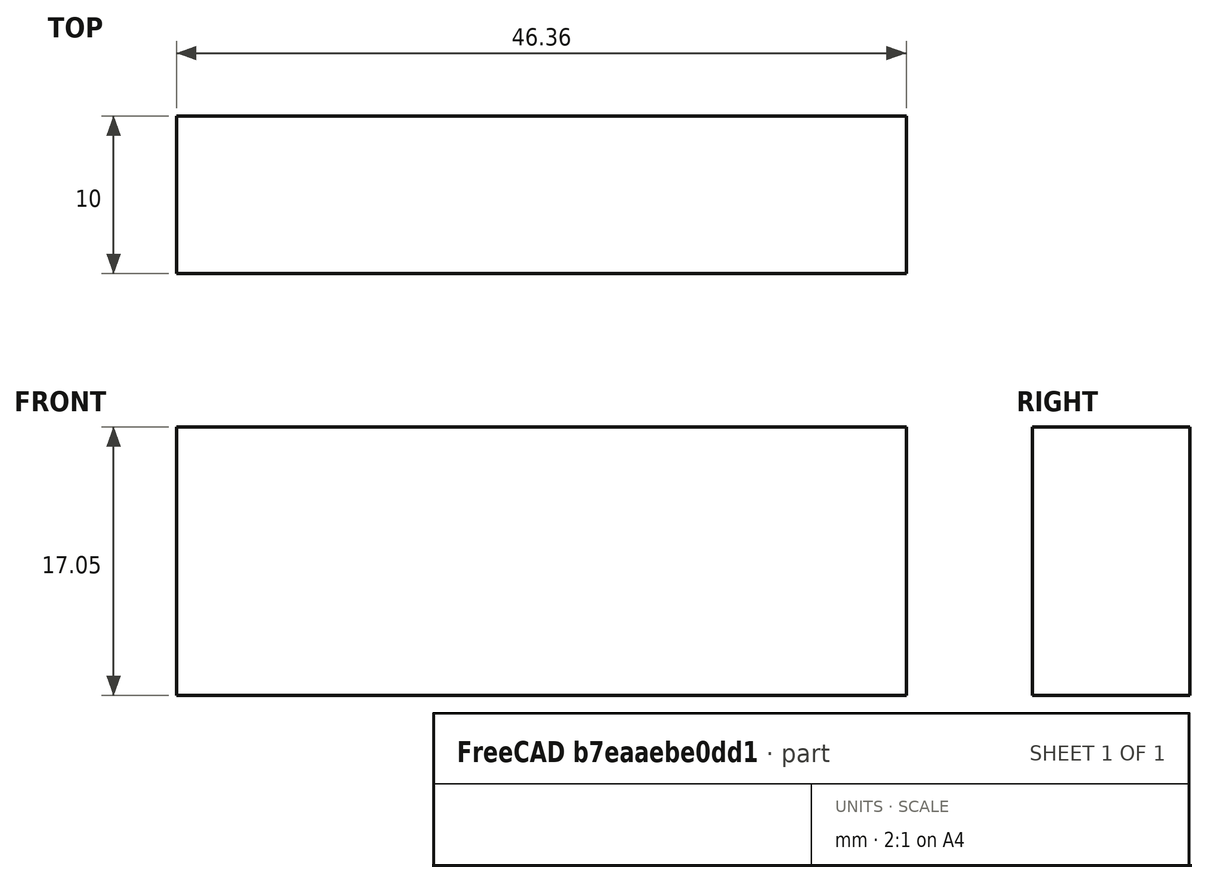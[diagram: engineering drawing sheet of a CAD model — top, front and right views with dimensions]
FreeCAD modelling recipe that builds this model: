
FCSTD DOCUMENT  (FreeCAD 0.21R33694 (Git))
Label: OJT1_T018_Tutorial
License: All rights reserved
LicenseURL: https://en.wikipedia.org/wiki/All_rights_reserved
objects: Sketcher::SketchObject×1, PartDesign::Pad×1, PartDesign::Body×1
note: 4 computed .brp shape members not serialized (recipe doc carries the construction recipe); baked Part::Feature solids carry a one-line shape summary decoded from their .brp

FEATURE [Sketcher::SketchObject] Sketch
  FullyConstrained = false
  MapMode = 5
  Placement = pos=(0,0,0) rot=(1,0,0;1.5708rad)
  Support = -> [XZ_Plane]
  sketch-geometry (4):
    g0: LineSegment StartX=-19.0953 StartY=21.9346 StartZ=0 EndX=-19.0953 EndY=4.88455 EndZ=0
    g1: LineSegment StartX=-19.0953 StartY=21.9346 StartZ=0 EndX=27.2647 EndY=21.9346 EndZ=0
    g2: LineSegment StartX=27.2647 StartY=21.9346 StartZ=0 EndX=27.2647 EndY=4.88455 EndZ=0
    g3: LineSegment StartX=-19.0953 StartY=4.88455 StartZ=0 EndX=27.2647 EndY=4.88455 EndZ=0
  constraints (10):
    c: Coincident(g0,g1)
    c: Coincident(g0,g3)
    c: Coincident(g1,g2)
    c: Coincident(g3,g2)
    c: Horizontal(g1)
    c: Vertical(g0)
    c: Vertical(g2)
    c: Horizontal(g3)
    c: DistanceY(g0,g0) = 17.05
    c: DistanceX(g1,g1) = 46.36
FEATURE [PartDesign::Pad] Pad
  Direction = (0,-1,2e-16)
  Length = 10
  Length2 = 10
  Placement = pos=(0,0,0) rot=(1,0,0;1.5708rad)
  Profile = -> Sketch
  ReferenceAxis = -> Sketch [N_Axis]
  Type = 0
FEATURE [PartDesign::Body] Body
  Group = -> [Sketch,Pad]
  Origin = -> Origin
  Tip = -> Pad
